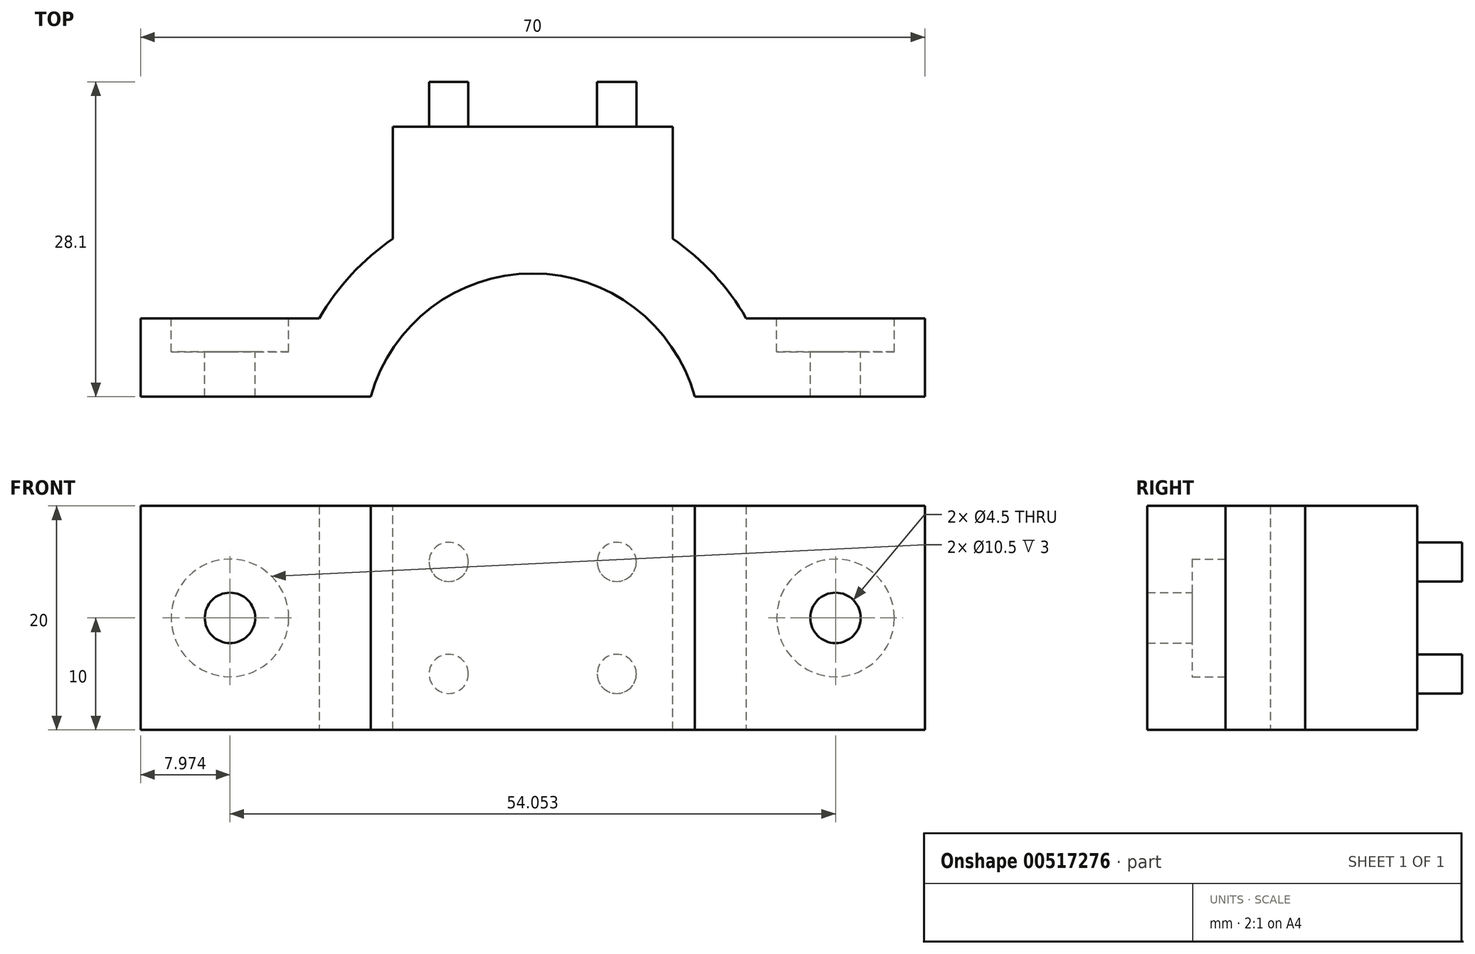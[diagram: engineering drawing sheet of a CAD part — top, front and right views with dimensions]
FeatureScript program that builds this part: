
annotation { "Feature Type Name" : "Feature", "Feature Type Description" : "" }
export const myFeature = defineFeature(function(context is Context, id is Id, definition is map)
    precondition{}
    {
        {
            var Q0;
            Q0=qCreatedBy(makeId("Top.planeOp"),FACE);
            var sketch = newSketch(context, id + "F0", { "sketchPlane" : qUnion([Q0])});
            skLineSegment(sketch, "E0", {"start": v(-35, 0) * mm, "end": v(-14.46, 0) * mm});
            skLineSegment(sketch, "E1.MirrorCS", {"start": v(35, 0) * mm, "end": v(14.46, 0) * mm});
            skArc(sketch, "E2", {"start": v(14.46, 0) * mm, "mid": v(0, 11) * mm, "end": v(-14.46, 0) * mm});
            skArc(sketch, "E3.0", {"start": v(19.05, 7) * mm, "mid": v(0, 18) * mm, "end": v(-19.05, 7) * mm});
            skLineSegment(sketch, "E4.0", {"start": v(-35, 7) * mm, "end": v(-19.05, 7) * mm});
            skLineSegment(sketch, "E5.MirrorCS", {"start": v(35, 7) * mm, "end": v(19.05, 7) * mm});
            skLineSegment(sketch, "E6.MirrorCS", {"start": v(35, 7) * mm, "end": v(35, 0) * mm});
            skLineSegment(sketch, "E7", {"start": v(-35, 7) * mm, "end": v(-35, 0) * mm});
            skSolve(sketch);
        }
        {
            var Q0;
            Q0=qSketchRegion(id+"F0",true);
            extrude(context, id + "F1", {"entities" : qUnion([Q0]), "endBound" : BoundingType.SYMMETRIC, "depth" : 20 * mm, "offsetDistance" : 25 * mm});
        }
        {
            var Q0;
            Q0=makeQuery(id+"F1.opExtrude","SWEPT_FACE",FACE,{"disambiguationData":[OSD([sQuery(id+"F0.wireOp",EDGE,"E5.MirrorCS")])]});
            var sketch = newSketch(context, id + "F2", { "sketchPlane" : qUnion([Q0])});
            skCircle(sketch, "E8", {"center": v(-27.03, 0) * mm, "radius": 2.25 * mm});
            skLineSegment(sketch, "E9", {"start": v(-27.03, 10) * mm, "end": v(-27.03, -10) * mm, "construction": true});
            skCircle(sketch, "E10.MirrorC", {"center": v(27.03, 0) * mm, "radius": 2.25 * mm});
            skSolve(sketch);
        }
        {
            var Q0;
            Q0=qSketchRegion(id+"F2",true);
            extrude(context, id + "F3", {"entities" : qUnion([Q0]), "operationType" : NewBodyOperationType.REMOVE, "oppositeDirection" : true, "depth" : 25 * mm, "offsetDistance" : 25 * mm});
        }
        {
            var Q0;
            Q0=makeQuery(id+"F1.opExtrude","SWEPT_FACE",FACE,{"disambiguationData":[OSD([sQuery(id+"F0.wireOp",EDGE,"E4.0")])]});
            var sketch = newSketch(context, id + "F4", { "sketchPlane" : qUnion([Q0])});
            skCircle(sketch, "E11.0", {"center": v(27.03, 0) * mm, "radius": 2.25 * mm});
            skCircle(sketch, "E12.0", {"center": v(27.03, 0) * mm, "radius": 5.25 * mm});
            skCircle(sketch, "E13.MirrorC", {"center": v(-27.03, 0) * mm, "radius": 5.25 * mm});
            skSolve(sketch);
        }
        {
            var Q0;
            Q0=qSketchRegion(id+"F4",true);
            extrude(context, id + "F5", {"entities" : qUnion([Q0]), "operationType" : NewBodyOperationType.REMOVE, "oppositeDirection" : true, "depth" : 3 * mm, "offsetDistance" : 25 * mm});
        }
        {
            var Q0;
            Q0=makeQuery(id+"F1.opExtrude","CAP_FACE",FACE,{"disambiguationData":[OSD([sQuery(id+"F0.wireOp",EDGE,"E0"),sQuery(id+"F0.wireOp",EDGE,"E1.MirrorCS"),sQuery(id+"F0.wireOp",EDGE,"E2"),sQuery(id+"F0.wireOp",EDGE,"E3.0"),sQuery(id+"F0.wireOp",EDGE,"E4.0"),sQuery(id+"F0.wireOp",EDGE,"E5.MirrorCS"),sQuery(id+"F0.wireOp",EDGE,"E6.MirrorCS"),sQuery(id+"F0.wireOp",EDGE,"E7")])],"isStart":false});
            var sketch = newSketch(context, id + "F6", { "sketchPlane" : qUnion([Q0])});
            skLineSegment(sketch, "E14.bottom", {"start": v(-12.5, 14.1) * mm, "end": v(12.5, 14.1) * mm});
            skLineSegment(sketch, "E14.top", {"start": v(-12.5, 24.1) * mm, "end": v(12.5, 24.1) * mm});
            skLineSegment(sketch, "E14.left", {"start": v(-12.5, 14.1) * mm, "end": v(-12.5, 24.1) * mm});
            skLineSegment(sketch, "E14.right", {"start": v(12.5, 14.1) * mm, "end": v(12.5, 24.1) * mm});
            skLineSegment(sketch, "E15", {"start": v(0, 24.1) * mm, "end": v(0, 14.1) * mm, "construction": true});
            skSolve(sketch);
        }
        {
            var Q0;
            Q0=qSketchRegion(id+"F6",true);
            extrude(context, id + "F7", {"entities" : qUnion([Q0]), "operationType" : NewBodyOperationType.ADD, "oppositeDirection" : true, "depth" : 20 * mm, "offsetDistance" : 25 * mm});
        }
        {
            var Q0;
            Q0=makeQuery(id+"F7.opExtrude","SWEPT_FACE",FACE,{"disambiguationData":[OSD([sQuery(id+"F6.wireOp",EDGE,"E14.top")])]});
            var sketch = newSketch(context, id + "F8", { "sketchPlane" : qUnion([Q0])});
            skLineSegment(sketch, "E16.0", {"start": v(7.5, 5) * mm, "end": v(-7.5, 5) * mm, "construction": true});
            skLineSegment(sketch, "E16.1", {"start": v(7.5, -5) * mm, "end": v(7.5, 5) * mm, "construction": true});
            skLineSegment(sketch, "E16.2", {"start": v(-7.5, -5) * mm, "end": v(7.5, -5) * mm, "construction": true});
            skLineSegment(sketch, "E16.3", {"start": v(-7.5, 5) * mm, "end": v(-7.5, -5) * mm, "construction": true});
            skCircle(sketch, "E17", {"center": v(7.5, -5) * mm, "radius": 1.75 * mm});
            skCircle(sketch, "E18.MirrorC", {"center": v(-7.5, -5) * mm, "radius": 1.75 * mm});
            skCircle(sketch, "E19.MirrorC", {"center": v(7.5, 5) * mm, "radius": 1.75 * mm});
            skCircle(sketch, "E20.MirrorC", {"center": v(-7.5, 5) * mm, "radius": 1.75 * mm});
            skSolve(sketch);
        }
        {
            var Q0;
            Q0=qSketchRegion(id+"F8",true);
            extrude(context, id + "F9", {"entities" : qUnion([Q0]), "operationType" : NewBodyOperationType.ADD, "depth" : 4 * mm, "offsetDistance" : 25 * mm});
        }
    });
